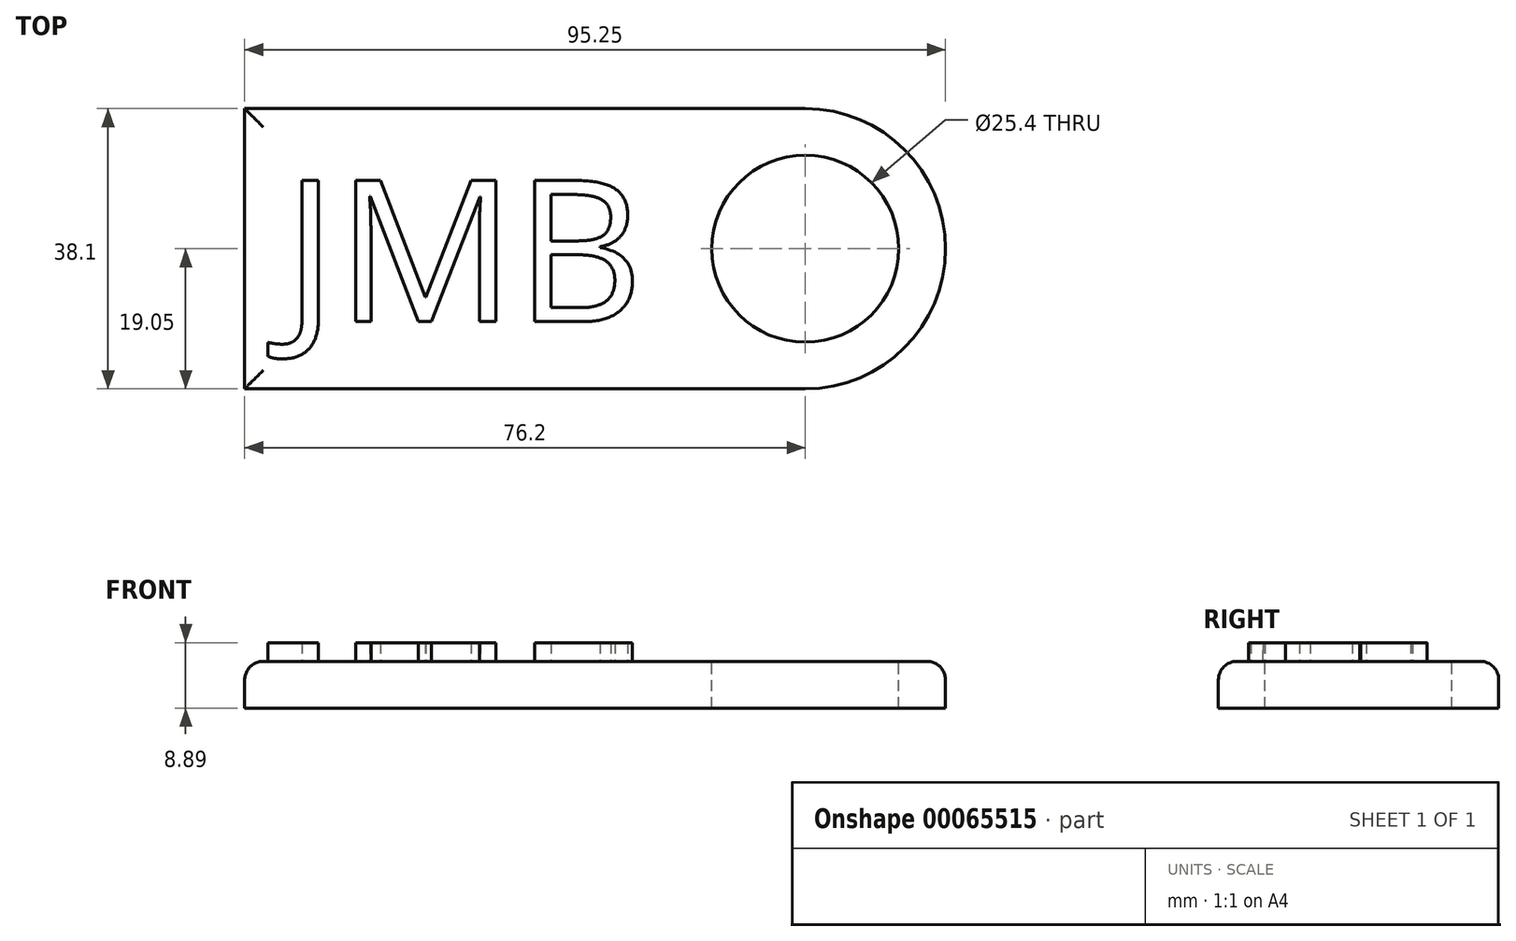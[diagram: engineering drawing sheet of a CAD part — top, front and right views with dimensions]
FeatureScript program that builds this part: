
annotation { "Feature Type Name" : "Feature", "Feature Type Description" : "" }
export const myFeature = defineFeature(function(context is Context, id is Id, definition is map)
    precondition{}
    {
        {
            var Q0;
            Q0=qCreatedBy(makeId("Top.planeOp"),FACE);
            var sketch = newSketch(context, id + "F0", { "sketchPlane" : qUnion([Q0])});
            skLineSegment(sketch, "E0.bottom", {"start": v(0, 0) * mm, "end": v(-76.2, 0) * mm});
            skLineSegment(sketch, "E0.top", {"start": v(0, 38.1) * mm, "end": v(-76.2, 38.1) * mm});
            skLineSegment(sketch, "E0.left", {"start": v(0, 0) * mm, "end": v(0, 38.1) * mm});
            skLineSegment(sketch, "E0.right", {"start": v(-76.2, 0) * mm, "end": v(-76.2, 38.1) * mm});
            skSolve(sketch);
        }
        {
            var Q0;
            Q0 = qSketchRegion(id + "F0", true);
            extrude(context, id + "F1", {"entities" : qUnion([Q0]), "depth" : 6.35 * mm});
        }
        {
            var Q0;
            Q0=makeQuery(id+"F1.opExtrude","CAP_FACE",FACE,{"disambiguationData":[OSD([sQuery(id+"F0.wireOp",EDGE,"E0.bottom"),sQuery(id+"F0.wireOp",EDGE,"E0.top"),sQuery(id+"F0.wireOp",EDGE,"E0.left"),sQuery(id+"F0.wireOp",EDGE,"E0.right")])],"isStart":false});
            var sketch = newSketch(context, id + "F2", { "sketchPlane" : qUnion([Q0])});
            skArc(sketch, "E1", {"start": v(0, 0) * mm, "mid": v(19.05, 19.05) * mm, "end": v(0, 38.1) * mm});
            skLineSegment(sketch, "E2", {"start": v(0, 38.1) * mm, "end": v(0, 0) * mm});
            skSolve(sketch);
        }
        {
            var Q0;
            Q0 = qSketchRegion(id + "F2", true);
            extrude(context, id + "F3", {"entities" : qUnion([Q0]), "operationType" : NewBodyOperationType.ADD, "oppositeDirection" : true, "depth" : 6.35 * mm});
        }
        {
            var Q0;
            Q0=makeQuery(id+"F3.boolean.opBoolean","MERGE",FACE,{"derivedFrom":[makeQuery(id+"F1.opExtrude","CAP_FACE",FACE,{"disambiguationData":[OSD([sQuery(id+"F0.wireOp",EDGE,"E0.bottom"),sQuery(id+"F0.wireOp",EDGE,"E0.top"),sQuery(id+"F0.wireOp",EDGE,"E0.left"),sQuery(id+"F0.wireOp",EDGE,"E0.right")])],"isStart":false}),makeQuery(id+"F3.opExtrude","CAP_FACE",FACE,{"disambiguationData":[OSD([sQuery(id+"F2.wireOp",EDGE,"E1"),sQuery(id+"F2.wireOp",EDGE,"E2")])],"isStart":true})]});
            var sketch = newSketch(context, id + "F4", { "sketchPlane" : qUnion([Q0])});
            skCircle(sketch, "E3", {"center": v(0, 19.05) * mm, "radius": 12.7 * mm});
            skSolve(sketch);
        }
        {
            var Q0;
            Q0 = qSketchRegion(id + "F4", true);
            extrude(context, id + "F5", {"entities" : qUnion([Q0]), "operationType" : NewBodyOperationType.REMOVE, "oppositeDirection" : true, "depth" : 6.35 * mm});
        }
        {
            var Q0;
            Q0=makeQuery(id+"F3.boolean.opBoolean","MERGE",FACE,{"derivedFrom":[makeQuery(id+"F1.opExtrude","CAP_FACE",FACE,{"disambiguationData":[OSD([sQuery(id+"F0.wireOp",EDGE,"E0.bottom"),sQuery(id+"F0.wireOp",EDGE,"E0.top"),sQuery(id+"F0.wireOp",EDGE,"E0.left"),sQuery(id+"F0.wireOp",EDGE,"E0.right")])],"isStart":false}),makeQuery(id+"F3.opExtrude","CAP_FACE",FACE,{"disambiguationData":[OSD([sQuery(id+"F2.wireOp",EDGE,"E1"),sQuery(id+"F2.wireOp",EDGE,"E2")])],"isStart":true})]});
            var sketch = newSketch(context, id + "F6", { "sketchPlane" : qUnion([Q0])});
            skText(sketch, "E4", { "text": "JMB", "fontName": "OpenSans-Regular.ttf"});
            const initialGuessF6  = {"E4": [-0.07092, 0.00913, 1, 0, 0.01937]};
            skSetInitialGuess(sketch, initialGuessF6);
            skSolve(sketch);
        }
        {
            var Q0;
            Q0 = qSketchRegion(id + "F6", true);
            extrude(context, id + "F7", {"entities" : qUnion([Q0]), "operationType" : NewBodyOperationType.ADD, "depth" : 2.54 * mm});
        }
        {
            var Q0;
            Q0=makeQuery(id+"F1.opExtrude","CAP_EDGE",EDGE,{"disambiguationData":[OSD([sQuery(id+"F0.wireOp",EDGE,"E0.bottom")])],"isStart":false});
            var Q1;
            Q1=makeQuery(id+"F1.opExtrude","CAP_EDGE",EDGE,{"disambiguationData":[OSD([sQuery(id+"F0.wireOp",EDGE,"E0.right")])],"isStart":false});
            fillet(context, id + "F8", {"entities" : qUnion([Q0, Q1]), "radius" : 2.54 * mm, "tangentPropagation" : true, "allowEdgeOverflow" : false});
        }
    });
